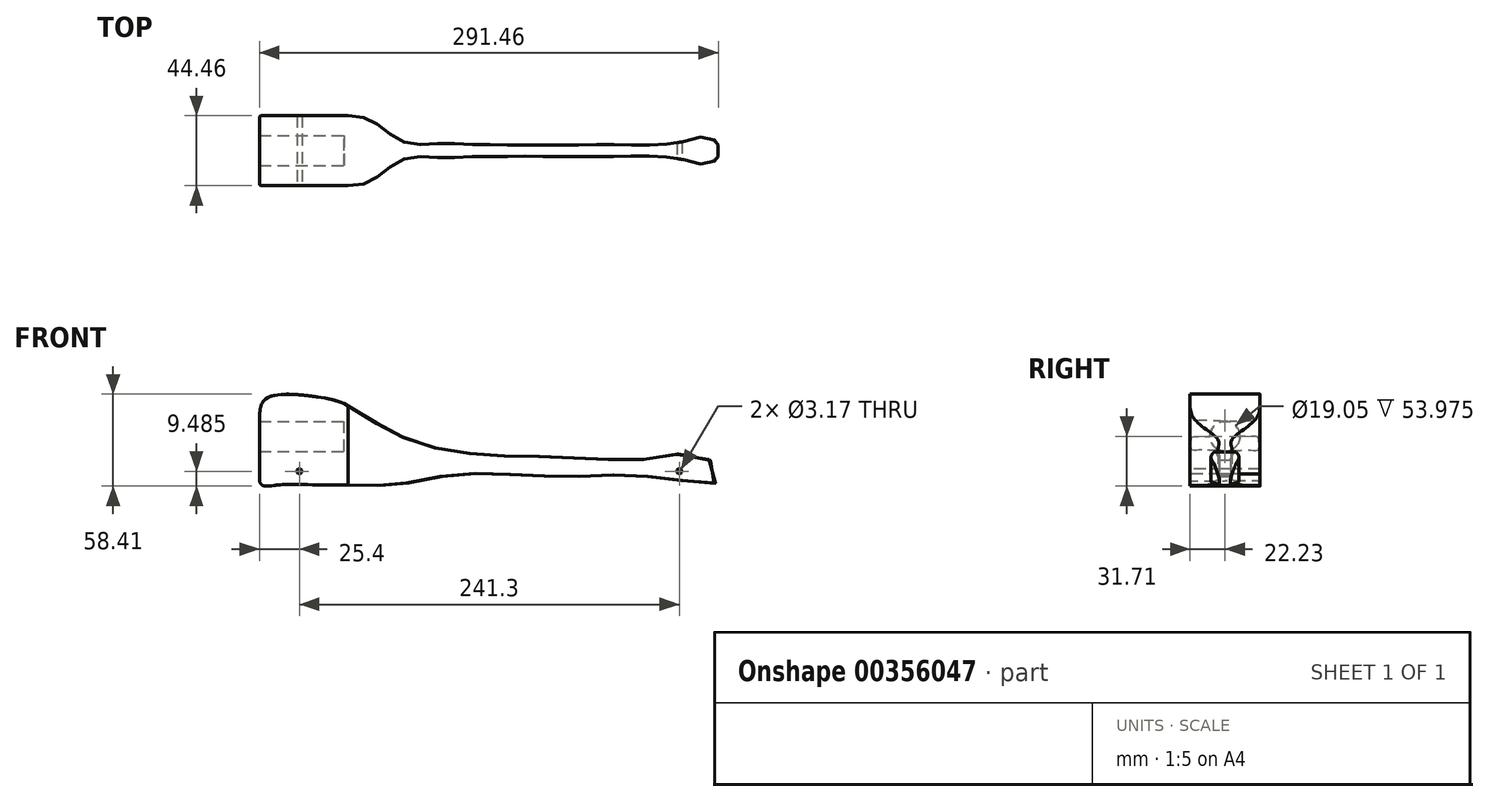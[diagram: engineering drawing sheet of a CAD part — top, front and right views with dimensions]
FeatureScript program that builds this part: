
annotation { "Feature Type Name" : "Feature", "Feature Type Description" : "" }
export const myFeature = defineFeature(function(context is Context, id is Id, definition is map)
    precondition{}
    {
        {
            var Q0;
            Q0=qCreatedBy(makeId("Front.planeOp"),FACE);
            var sketch = newSketch(context, id + "F0", { "sketchPlane" : qUnion([Q0])});
            skLineSegment(sketch, "E0.bottom", {"start": v(-146.05, 31.75) * mm, "end": v(146.05, 31.75) * mm, "construction": true});
            skLineSegment(sketch, "E0.top", {"start": v(-146.05, -31.75) * mm, "end": v(146.05, -31.75) * mm, "construction": true});
            skLineSegment(sketch, "E0.right", {"start": v(146.05, 31.75) * mm, "end": v(146.05, -31.75) * mm, "construction": true});
            skFitSpline(sketch, "E1", {"points": [v(-146.05, -8.99) * mm, v(-146.05, 0) * mm, v(-146.05, 9.53) * mm, v(-144.32, 21.05) * mm, v(-138.76, 25.38) * mm, v(-127.7, 26.7) * mm, v(-115.3, 25.77) * mm, v(-103.46, 24.05) * mm, v(-90.13, 19.66) * mm, v(-63.73, 3.76) * mm, v(-29.48, -8.51) * mm, v(5.34, -12.26) * mm, v(34.93, -12.85) * mm, v(110.17, -13.67) * mm, v(127.5, -10.03) * mm, v(140.72, -15.54) * mm, v(143.22, -18.53) * mm, v(145.4, -28.68) * mm, v(144.96, -31.14) * mm, v(144.78, -30.48) * mm, v(125.33, -28.38) * mm, v(89.52, -24.7) * mm, v(63.08, -25.39) * mm, v(42.63, -25.39) * mm, v(15.53, -24.24) * mm, v(-9.74, -23.78) * mm, v(-29.96, -25.39) * mm, v(-60, -30.8) * mm, v(-90.1, -30.87) * mm, v(-110.02, -30.87) * mm, v(-135.61, -31.07) * mm, v(-145.23, -30.14) * mm, v(-146.05, -8.99) * mm]});
            skLineSegment(sketch, "E2.bottom", {"start": v(-146.05, 9.52) * mm, "end": v(-95.25, 9.52) * mm, "construction": true});
            skLineSegment(sketch, "E2.top", {"start": v(-141.83, -9.52) * mm, "end": v(-95.25, -9.52) * mm, "construction": true});
            skLineSegment(sketch, "E2.right", {"start": v(-95.25, 9.52) * mm, "end": v(-95.25, -9.52) * mm, "construction": true});
            skLineSegment(sketch, "E3", {"start": v(-146.05, 31.75) * mm, "end": v(-146.05, -31.75) * mm, "construction": true});
            skSolve(sketch);
        }
        {
            var Q0;
            Q0=qCreatedBy(makeId("Top.planeOp"),FACE);
            var sketch = newSketch(context, id + "F1", { "sketchPlane" : qUnion([Q0])});
            skLineSegment(sketch, "E4.bottom", {"start": v(-146.05, 22.22) * mm, "end": v(146.05, 22.23) * mm, "construction": true});
            skLineSegment(sketch, "E4.top", {"start": v(-146.05, -22.23) * mm, "end": v(146.05, -22.22) * mm, "construction": true});
            skLineSegment(sketch, "E4.left", {"start": v(-146.05, 22.22) * mm, "end": v(-146.05, -22.23) * mm, "construction": true});
            skLineSegment(sketch, "E4.right", {"start": v(146.05, 22.22) * mm, "end": v(146.05, -22.22) * mm, "construction": true});
            skLineSegment(sketch, "E5", {"start": v(-146.05, 0) * mm, "end": v(146.05, 0) * mm, "construction": true});
            skFitSpline(sketch, "E6", {"points": [v(-146.05, 0) * mm, v(-146.05, 19.96) * mm, v(-145.72, 21.88) * mm, v(-142.18, 22.22) * mm, v(-116.53, 22.22) * mm, v(-93.48, 22.22) * mm, v(-75.72, 19.46) * mm, v(-54.35, 5.4) * mm, v(-33.61, 4.4) * mm, v(-14.79, 4.02) * mm, v(0, 3.8) * mm, v(14.02, 3.62) * mm, v(33.56, 3.62) * mm, v(60.87, 3.71) * mm, v(83.8, 3.71) * mm, v(106.06, 3.71) * mm, v(126.25, 6.45) * mm, v(136.18, 8.85) * mm, v(142, 7.48) * mm, v(146.05, 0) * mm], "startDerivative": vector(0, 257.96) * mm, "endDerivative": vector(0, -277.49) * mm});
            skFitSpline(sketch, "E7.MirrorCS", {"points": [v(-146.05, 0) * mm, v(-146.05, -19.96) * mm, v(-145.72, -21.88) * mm, v(-142.18, -22.23) * mm, v(-116.53, -22.23) * mm, v(-93.48, -22.23) * mm, v(-75.72, -19.46) * mm, v(-54.35, -5.4) * mm, v(-33.61, -4.4) * mm, v(-14.79, -4.02) * mm, v(0, -3.8) * mm, v(14.02, -3.62) * mm, v(33.56, -3.62) * mm, v(60.87, -3.71) * mm, v(83.8, -3.71) * mm, v(106.06, -3.71) * mm, v(126.25, -6.45) * mm, v(136.18, -8.85) * mm, v(142, -7.48) * mm, v(146.05, 0) * mm], "startDerivative": vector(0, -257.96) * mm, "endDerivative": vector(0, 277.49) * mm});
            skLineSegment(sketch, "E8.MirrorCS", {"start": v(-146.05, -22.23) * mm, "end": v(146.05, -22.23) * mm});
            skSolve(sketch);
        }
        {
            var Q0;
            Q0=qCreatedBy(makeId("Right.planeOp"),FACE);
            var sketch = newSketch(context, id + "F2", { "sketchPlane" : qUnion([Q0])});
            skCircle(sketch, "E9", {"center": v(0, 0) * mm, "radius": 9.53 * mm});
            skSolve(sketch);
        }
        {
            var Q0;
            Q0=qCreatedBy(makeId("Front.planeOp"),FACE);
            var sketch = newSketch(context, id + "F3", { "sketchPlane" : qUnion([Q0])});
            skCircle(sketch, "E10", {"center": v(-120.65, -22.22) * mm, "radius": 1.59 * mm});
            skCircle(sketch, "E11", {"center": v(120.65, -22.23) * mm, "radius": 1.59 * mm});
            skSolve(sketch);
        }
        {
            var Q0;
            Q0=qSketchRegion(id+"F0",true);
            extrude(context, id + "F4", {"entities" : qUnion([Q0]), "depth" : 44.45 * mm, "symmetric" : true});
        }
        {
            var Q0;
            Q0=qSketchRegion(id+"F1",true);
            extrude(context, id + "F5", {"entities" : qUnion([Q0]), "operationType" : NewBodyOperationType.INTERSECT, "endBound" : BoundingType.THROUGH_ALL, "oppositeDirection" : true, "depth" : 60.96 * mm, "hasSecondDirection" : true, "secondDirectionBound" : BoundingType.THROUGH_ALL, "secondDirectionOppositeDirection" : false, "secondDirectionDepth" : 25.4 * mm});
        }
        {
            var Q0;
            Q0=qSketchRegion(id+"F2",true);
            extrude(context, id + "F6", {"entities" : qUnion([Q0]), "operationType" : NewBodyOperationType.REMOVE, "oppositeDirection" : true, "depth" : 152.4 * mm, "hasSecondDirection" : true, "secondDirectionOppositeDirection" : true, "secondDirectionDepth" : 92.07 * mm});
        }
        {
            var Q0;
            Q0=qSketchRegion(id+"F3",true);
            extrude(context, id + "F7", {"entities" : qUnion([Q0]), "operationType" : NewBodyOperationType.REMOVE, "oppositeDirection" : true, "depth" : 50.8 * mm, "symmetric" : true});
        }
    });
